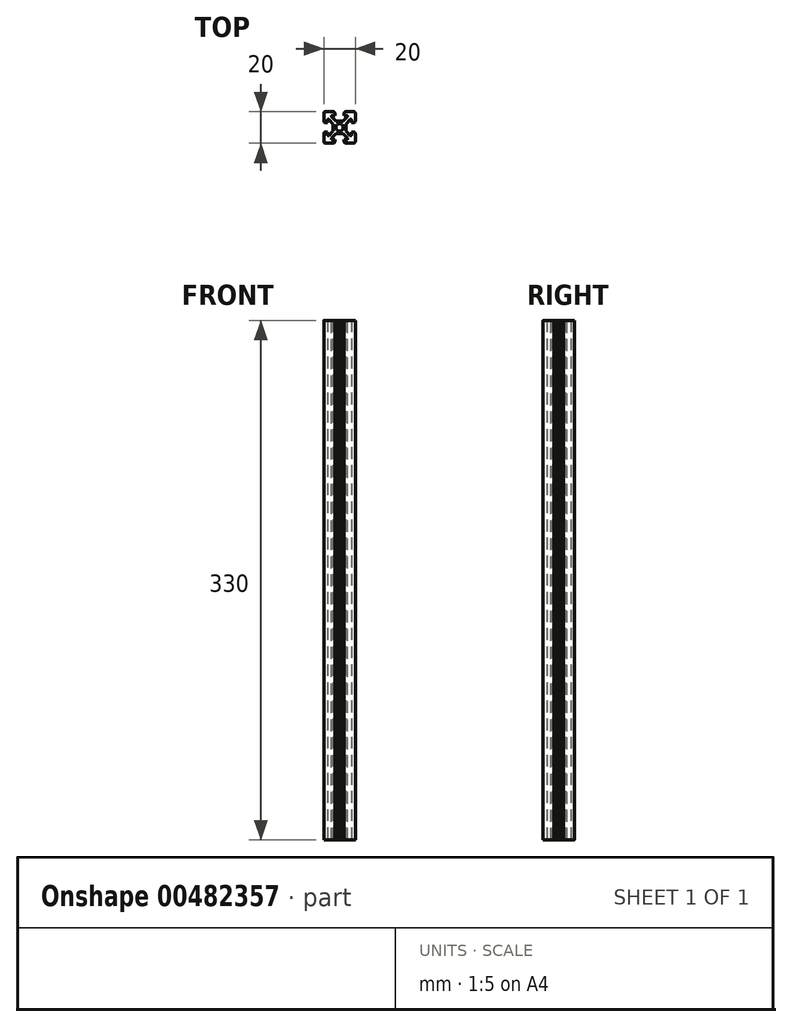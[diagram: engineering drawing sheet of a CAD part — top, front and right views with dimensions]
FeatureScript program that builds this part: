
annotation { "Feature Type Name" : "Feature", "Feature Type Description" : "" }
export const myFeature = defineFeature(function(context is Context, id is Id, definition is map)
    precondition{}
    {
        {
            var Q0;
            Q0=qCreatedBy(makeId("Top.planeOp"),FACE);
            var sketch = newSketch(context, id + "F0", { "sketchPlane" : qUnion([Q0])});
            skLineSegment(sketch, "E0", {"start": v(-15.81, 0) * mm, "end": v(2.4, 0) * mm, "construction": true});
            skLineSegment(sketch, "E1", {"start": v(0, 15.89) * mm, "end": v(0, -13.7) * mm, "construction": true});
            skLineSegment(sketch, "E2", {"start": v(0, 0) * mm, "end": v(-1.66, 1.66) * mm, "construction": true});
            skLineSegment(sketch, "E3", {"start": v(-2.3, 4.06) * mm, "end": v(-5.86, 7.63) * mm});
            skLineSegment(sketch, "E4", {"start": v(-5.86, 7.63) * mm, "end": v(-3, 7.63) * mm});
            skLineSegment(sketch, "E5", {"start": v(-3, 7.63) * mm, "end": v(-3, 10) * mm});
            skLineSegment(sketch, "E6", {"start": v(-3, 10) * mm, "end": v(-10, 10) * mm});
            skLineSegment(sketch, "E7.MirrorCS", {"start": v(-4, 2.23) * mm, "end": v(-7.63, 5.86) * mm});
            skLineSegment(sketch, "E8.MirrorCS", {"start": v(-7.63, 3) * mm, "end": v(-10, 3) * mm});
            skLineSegment(sketch, "E9.MirrorCS", {"start": v(-10, 3) * mm, "end": v(-10, 10) * mm});
            skLineSegment(sketch, "E10.MirrorCS", {"start": v(-7.63, 5.86) * mm, "end": v(-7.63, 3) * mm});
            skLineSegment(sketch, "E11.MirrorCS", {"start": v(3, 10) * mm, "end": v(10, 10) * mm});
            skLineSegment(sketch, "E12.MirrorCS", {"start": v(5.86, 7.63) * mm, "end": v(3, 7.63) * mm});
            skLineSegment(sketch, "E13.MirrorCS", {"start": v(3, 7.63) * mm, "end": v(3, 10) * mm});
            skLineSegment(sketch, "E14.MirrorCS", {"start": v(7.63, 5.86) * mm, "end": v(7.63, 3) * mm});
            skLineSegment(sketch, "E15.MirrorCS", {"start": v(10, 3) * mm, "end": v(10, 10) * mm});
            skLineSegment(sketch, "E16.MirrorCS", {"start": v(7.63, 3) * mm, "end": v(10, 3) * mm});
            skLineSegment(sketch, "E17.MirrorCS", {"start": v(2.3, 4.06) * mm, "end": v(5.86, 7.63) * mm});
            skLineSegment(sketch, "E18.MirrorCS", {"start": v(4, 2.23) * mm, "end": v(7.63, 5.86) * mm});
            skLineSegment(sketch, "E19.MirrorCS", {"start": v(5.86, -7.63) * mm, "end": v(3, -7.63) * mm});
            skLineSegment(sketch, "E20.MirrorCS", {"start": v(3, -10) * mm, "end": v(10, -10) * mm});
            skLineSegment(sketch, "E21.MirrorCS", {"start": v(-5.86, -7.63) * mm, "end": v(-3, -7.63) * mm});
            skLineSegment(sketch, "E22.MirrorCS", {"start": v(-3, -10) * mm, "end": v(-10, -10) * mm});
            skLineSegment(sketch, "E23.MirrorCS", {"start": v(-3, -7.63) * mm, "end": v(-3, -10) * mm});
            skLineSegment(sketch, "E24.MirrorCS", {"start": v(3, -7.63) * mm, "end": v(3, -10) * mm});
            skLineSegment(sketch, "E25.MirrorCS", {"start": v(7.63, -5.86) * mm, "end": v(7.63, -3) * mm});
            skLineSegment(sketch, "E26.MirrorCS", {"start": v(10, -3) * mm, "end": v(10, -10) * mm});
            skLineSegment(sketch, "E27.MirrorCS", {"start": v(4, -2.23) * mm, "end": v(7.63, -5.86) * mm});
            skLineSegment(sketch, "E28.MirrorCS", {"start": v(-7.63, -5.86) * mm, "end": v(-7.63, -3) * mm});
            skLineSegment(sketch, "E29.MirrorCS", {"start": v(-10, -3) * mm, "end": v(-10, -10) * mm});
            skLineSegment(sketch, "E30.MirrorCS", {"start": v(-7.63, -3) * mm, "end": v(-10, -3) * mm});
            skLineSegment(sketch, "E31.MirrorCS", {"start": v(-4, -2.23) * mm, "end": v(-7.63, -5.86) * mm});
            skLineSegment(sketch, "E32.MirrorCS", {"start": v(2.23, -4) * mm, "end": v(5.86, -7.63) * mm});
            skLineSegment(sketch, "E33.MirrorCS", {"start": v(-2.23, -4) * mm, "end": v(-5.86, -7.63) * mm});
            skLineSegment(sketch, "E34.MirrorCS", {"start": v(7.63, -3) * mm, "end": v(10, -3) * mm});
            skLineSegment(sketch, "E35", {"start": v(-4, 0) * mm, "end": v(-4, 0) * mm});
            skLineSegment(sketch, "E36", {"start": v(-2.3, 4.06) * mm, "end": v(-0.02, 4.06) * mm});
            skLineSegment(sketch, "E37.MirrorCS", {"start": v(-15.81, 8.12) * mm, "end": v(21.32, 8.12) * mm, "construction": true});
            skLineSegment(sketch, "E38", {"start": v(-4, 2.23) * mm, "end": v(-4, 0.02) * mm});
            skLineSegment(sketch, "E39", {"start": v(-2.23, -4) * mm, "end": v(-0.05, -4) * mm});
            skLineSegment(sketch, "E40", {"start": v(4, 2.23) * mm, "end": v(4, 0.03) * mm});
            skPoint(sketch, "E41.orphan", {"position": v(-0.59, 2.36) * mm});
            skPoint(sketch, "E42.orphan", {"position": v(-2.36, 0.59) * mm});
            skLineSegment(sketch, "E43.trimOffspring", {"start": v(0.03, 4.06) * mm, "end": v(2.3, 4.06) * mm});
            skPoint(sketch, "E44.orphan", {"position": v(0.59, 2.36) * mm});
            skPoint(sketch, "E45.orphan", {"position": v(2.36, 0.59) * mm});
            skPoint(sketch, "E46.orphan", {"position": v(-2.36, -0.59) * mm});
            skPoint(sketch, "E47.orphan", {"position": v(-0.59, -2.36) * mm});
            skPoint(sketch, "E48.orphan", {"position": v(0.59, -2.36) * mm});
            skPoint(sketch, "E49.orphan", {"position": v(2.36, -0.59) * mm});
            skLineSegment(sketch, "E50", {"start": v(-2.4, 0.03) * mm, "end": v(-2.4, 0.03) * mm});
            skLineSegment(sketch, "E51.MirrorCS", {"start": v(-2.4, -0.03) * mm, "end": v(-2.4, -0.03) * mm});
            skLineSegment(sketch, "E52.MirrorCS", {"start": v(2.4, 0.03) * mm, "end": v(2.4, 0.03) * mm});
            skLineSegment(sketch, "E53.MirrorCS", {"start": v(2.4, -0.03) * mm, "end": v(2.4, -0.03) * mm});
            skLineSegment(sketch, "E54.trimOffspring", {"start": v(4, -0.03) * mm, "end": v(4, -2.23) * mm});
            skLineSegment(sketch, "E55.trimOffspring", {"start": v(-4, -0.03) * mm, "end": v(-4, -2.23) * mm});
            skPoint(sketch, "E56.end.orphan", {"position": v(-2.4, 0) * mm});
            skPoint(sketch, "E57.orphan", {"position": v(-4, 0.03) * mm});
            skPoint(sketch, "E58.MirrorCS.end.orphan", {"position": v(2.4, 0) * mm});
            skPoint(sketch, "E58.MirrorCS.start.orphan", {"position": v(2.4, -0.03) * mm});
            skPoint(sketch, "E59.MirrorCS.start.orphan", {"position": v(2.4, 0.03) * mm});
            skLineSegment(sketch, "E60.trimOffspring", {"start": v(0.05, -4) * mm, "end": v(2.23, -4) * mm});
            skLineSegment(sketch, "E61", {"start": v(0, 0) * mm, "end": v(10, 10) * mm, "construction": true});
            skLineSegment(sketch, "E62", {"start": v(0, 0) * mm, "end": v(-10, -10) * mm, "construction": true});
            skLineSegment(sketch, "E63", {"start": v(10, -10) * mm, "end": v(0.07, 0.07) * mm, "construction": true});
            skPoint(sketch, "E64.start.orphan", {"position": v(-4, -0.03) * mm});
            skLineSegment(sketch, "E65", {"start": v(-2.82, -0.78) * mm, "end": v(-1.9, -1.37) * mm});
            skPoint(sketch, "E66.orphan", {"position": v(-1.66, -1.66) * mm});
            skPoint(sketch, "E67.orphan", {"position": v(0.03, -4.06) * mm});
            skPoint(sketch, "E68.orphan", {"position": v(-0.03, -4.06) * mm});
            skLineSegment(sketch, "E69", {"start": v(-2.82, 0.8) * mm, "end": v(-1.87, 1.41) * mm});
            skLineSegment(sketch, "E70", {"start": v(-0.76, 2.95) * mm, "end": v(-1.54, 1.77) * mm});
            skLineSegment(sketch, "E71", {"start": v(0.76, 2.95) * mm, "end": v(1.51, 1.8) * mm});
            skLineSegment(sketch, "E72", {"start": v(2.82, 0.8) * mm, "end": v(1.83, 1.46) * mm});
            skLineSegment(sketch, "E73", {"start": v(2.82, -0.8) * mm, "end": v(1.87, -1.41) * mm});
            skLineSegment(sketch, "E74.trimOffspring", {"start": v(1.8, -1.68) * mm, "end": v(1.82, -1.66) * mm});
            skLineSegment(sketch, "E75.trimOffspring", {"start": v(-8.12, 8.12) * mm, "end": v(-29.35, 29.35) * mm, "construction": true});
            skLineSegment(sketch, "E76", {"start": v(0.74, -2.96) * mm, "end": v(1.51, -1.8) * mm});
            skPoint(sketch, "E77.trimOffspring.start.orphan", {"position": v(0.33, -2.4) * mm});
            skPoint(sketch, "E78.MirrorCS.end.orphan", {"position": v(-0.33, -2.4) * mm});
            skLineSegment(sketch, "E79.trimOffspring", {"start": v(2.43, 0) * mm, "end": v(21.32, 0) * mm, "construction": true});
            skPoint(sketch, "E80.trimOffspring.start.orphan", {"position": v(0.33, 2.4) * mm});
            skPoint(sketch, "E81.trimOffspring.start.orphan", {"position": v(-0.33, 2.4) * mm});
            skArc(sketch, "E82", {"start": v(-1.87, 1.41) * mm, "mid": v(-2.35, 0.03) * mm, "end": v(-1.9, -1.37) * mm});
            skArc(sketch, "E83.trimOffspring", {"start": v(1.51, 1.8) * mm, "mid": v(-0.02, 2.35) * mm, "end": v(-1.54, 1.77) * mm});
            skArc(sketch, "E84.trimOffspring", {"start": v(1.87, -1.41) * mm, "mid": v(2.35, 0.03) * mm, "end": v(1.83, 1.46) * mm});
            skArc(sketch, "E85.trimOffspring", {"start": v(-1.55, -1.76) * mm, "mid": v(-0.03, -2.35) * mm, "end": v(1.51, -1.8) * mm});
            skLineSegment(sketch, "E86", {"start": v(-1.55, -1.76) * mm, "end": v(-0.75, -2.96) * mm});
            skLineSegment(sketch, "E87", {"start": v(-4, 0.03) * mm, "end": v(-2.82, 0.03) * mm});
            skLineSegment(sketch, "E88", {"start": v(-2.82, 0.03) * mm, "end": v(-2.82, 0.8) * mm});
            skLineSegment(sketch, "E89", {"start": v(-4, -0.03) * mm, "end": v(-2.82, -0.03) * mm});
            skLineSegment(sketch, "E90", {"start": v(-2.82, -0.03) * mm, "end": v(-2.82, -0.78) * mm});
            skLineSegment(sketch, "E91.MirrorCS", {"start": v(4, 0.03) * mm, "end": v(2.82, 0.03) * mm});
            skLineSegment(sketch, "E92.MirrorCS", {"start": v(4, -0.03) * mm, "end": v(2.82, -0.03) * mm});
            skLineSegment(sketch, "E93", {"start": v(2.82, 0.03) * mm, "end": v(2.82, 0.8) * mm});
            skLineSegment(sketch, "E94", {"start": v(2.82, -0.03) * mm, "end": v(2.82, -0.8) * mm});
            skLineSegment(sketch, "E95", {"start": v(-0.05, -4) * mm, "end": v(-0.05, -2.96) * mm});
            skLineSegment(sketch, "E96", {"start": v(-0.05, -2.96) * mm, "end": v(-0.75, -2.96) * mm});
            skLineSegment(sketch, "E97", {"start": v(0.05, -4) * mm, "end": v(0.05, -2.96) * mm});
            skLineSegment(sketch, "E98", {"start": v(0.05, -2.96) * mm, "end": v(0.74, -2.96) * mm});
            skLineSegment(sketch, "E99", {"start": v(-0.02, 4.06) * mm, "end": v(-0.02, 2.95) * mm});
            skLineSegment(sketch, "E100", {"start": v(-0.02, 2.95) * mm, "end": v(-0.76, 2.95) * mm});
            skLineSegment(sketch, "E101", {"start": v(0.03, 4.06) * mm, "end": v(0.03, 2.95) * mm});
            skLineSegment(sketch, "E102", {"start": v(0.03, 2.95) * mm, "end": v(0.76, 2.95) * mm});
            skSolve(sketch);
        }
        {
            var Q0;
            Q0 = qSketchRegion(id + "F0", true);
            extrude(context, id + "F1", {"entities" : qUnion([Q0]), "depth" : 330 * mm});
        }
        {
            var Q0;
            Q0=makeQuery(id+"F1.opExtrude","SWEPT_EDGE",EDGE,{"disambiguationData":[OSD([sQuery(id+"F0.wireOp",EDGE,"E15.MirrorCS"),sQuery(id+"F0.wireOp",EDGE,"E11.MirrorCS")])]});
            var Q1;
            Q1=makeQuery(id+"F1.opExtrude","SWEPT_EDGE",EDGE,{"disambiguationData":[OSD([sQuery(id+"F0.wireOp",EDGE,"E20.MirrorCS"),sQuery(id+"F0.wireOp",EDGE,"E26.MirrorCS")])]});
            var Q2;
            Q2=makeQuery(id+"F1.opExtrude","SWEPT_EDGE",EDGE,{"disambiguationData":[OSD([sQuery(id+"F0.wireOp",EDGE,"E22.MirrorCS"),sQuery(id+"F0.wireOp",EDGE,"E29.MirrorCS")])]});
            var Q3;
            Q3=makeQuery(id+"F1.opExtrude","SWEPT_EDGE",EDGE,{"disambiguationData":[OSD([sQuery(id+"F0.wireOp",EDGE,"E22.MirrorCS"),sQuery(id+"F0.wireOp",EDGE,"E23.MirrorCS")])]});
            var Q4;
            Q4=makeQuery(id+"F1.opExtrude","SWEPT_EDGE",EDGE,{"disambiguationData":[OSD([sQuery(id+"F0.wireOp",EDGE,"E20.MirrorCS"),sQuery(id+"F0.wireOp",EDGE,"E24.MirrorCS")])]});
            var Q5;
            Q5=makeQuery(id+"F1.opExtrude","SWEPT_EDGE",EDGE,{"disambiguationData":[OSD([sQuery(id+"F0.wireOp",EDGE,"E5"),sQuery(id+"F0.wireOp",EDGE,"E6")])]});
            var Q6;
            Q6=makeQuery(id+"F1.opExtrude","SWEPT_EDGE",EDGE,{"disambiguationData":[OSD([sQuery(id+"F0.wireOp",EDGE,"E8.MirrorCS"),sQuery(id+"F0.wireOp",EDGE,"E9.MirrorCS")])]});
            var Q7;
            Q7=makeQuery(id+"F1.opExtrude","SWEPT_EDGE",EDGE,{"disambiguationData":[OSD([sQuery(id+"F0.wireOp",EDGE,"E15.MirrorCS"),sQuery(id+"F0.wireOp",EDGE,"E16.MirrorCS")])]});
            var Q8;
            Q8=makeQuery(id+"F1.opExtrude","SWEPT_EDGE",EDGE,{"disambiguationData":[OSD([sQuery(id+"F0.wireOp",EDGE,"E26.MirrorCS"),sQuery(id+"F0.wireOp",EDGE,"E34.MirrorCS")])]});
            var Q9;
            Q9=makeQuery(id+"F1.opExtrude","SWEPT_EDGE",EDGE,{"disambiguationData":[OSD([sQuery(id+"F0.wireOp",EDGE,"E29.MirrorCS"),sQuery(id+"F0.wireOp",EDGE,"E30.MirrorCS")])]});
            var Q10;
            Q10=makeQuery(id+"F1.opExtrude","SWEPT_EDGE",EDGE,{"disambiguationData":[OSD([sQuery(id+"F0.wireOp",EDGE,"E9.MirrorCS"),sQuery(id+"F0.wireOp",EDGE,"E6")])]});
            var Q11;
            Q11=makeQuery(id+"F1.opExtrude","SWEPT_EDGE",EDGE,{"disambiguationData":[OSD([sQuery(id+"F0.wireOp",EDGE,"E13.MirrorCS"),sQuery(id+"F0.wireOp",EDGE,"E11.MirrorCS")])]});
            fillet(context, id + "F2", {"entities" : qUnion([Q0, Q1, Q2, Q3, Q4, Q5, Q6, Q7, Q8, Q9, Q10, Q11]), "radius" : 1 * mm, "tangentPropagation" : true, "allowEdgeOverflow" : false});
        }
        {
            var Q0;
            Q0=makeQuery(id+"F1.opExtrude","SWEPT_EDGE",EDGE,{"disambiguationData":[OSD([sQuery(id+"F0.wireOp",EDGE,"E7.MirrorCS"),sQuery(id+"F0.wireOp",EDGE,"E10.MirrorCS")])]});
            var Q1;
            Q1=makeQuery(id+"F1.opExtrude","SWEPT_EDGE",EDGE,{"disambiguationData":[OSD([sQuery(id+"F0.wireOp",EDGE,"E3"),sQuery(id+"F0.wireOp",EDGE,"E4")])]});
            var Q2;
            Q2=makeQuery(id+"F1.opExtrude","SWEPT_EDGE",EDGE,{"disambiguationData":[OSD([sQuery(id+"F0.wireOp",EDGE,"E12.MirrorCS"),sQuery(id+"F0.wireOp",EDGE,"E17.MirrorCS")])]});
            var Q3;
            Q3=makeQuery(id+"F1.opExtrude","SWEPT_EDGE",EDGE,{"disambiguationData":[OSD([sQuery(id+"F0.wireOp",EDGE,"E14.MirrorCS"),sQuery(id+"F0.wireOp",EDGE,"E18.MirrorCS")])]});
            var Q4;
            Q4=makeQuery(id+"F1.opExtrude","SWEPT_EDGE",EDGE,{"disambiguationData":[OSD([sQuery(id+"F0.wireOp",EDGE,"E28.MirrorCS"),sQuery(id+"F0.wireOp",EDGE,"E31.MirrorCS")])]});
            var Q5;
            Q5=makeQuery(id+"F1.opExtrude","SWEPT_EDGE",EDGE,{"disambiguationData":[OSD([sQuery(id+"F0.wireOp",EDGE,"E21.MirrorCS"),sQuery(id+"F0.wireOp",EDGE,"E33.MirrorCS")])]});
            var Q6;
            Q6=makeQuery(id+"F1.opExtrude","SWEPT_EDGE",EDGE,{"disambiguationData":[OSD([sQuery(id+"F0.wireOp",EDGE,"E19.MirrorCS"),sQuery(id+"F0.wireOp",EDGE,"E32.MirrorCS")])]});
            var Q7;
            Q7=makeQuery(id+"F1.opExtrude","SWEPT_EDGE",EDGE,{"disambiguationData":[OSD([sQuery(id+"F0.wireOp",EDGE,"E25.MirrorCS"),sQuery(id+"F0.wireOp",EDGE,"E27.MirrorCS")])]});
            fillet(context, id + "F3", {"entities" : qUnion([Q0, Q1, Q2, Q3, Q4, Q5, Q6, Q7]), "radius" : .5 * mm, "tangentPropagation" : true, "allowEdgeOverflow" : false});
        }
        {
            var Q0;
            Q0=makeQuery(id+"F1.opExtrude","SWEPT_EDGE",EDGE,{"disambiguationData":[OSD([sQuery(id+"F0.wireOp",EDGE,"E69"),sQuery(id+"F0.wireOp",EDGE,"E82")])]});
            var Q1;
            Q1=makeQuery(id+"F1.opExtrude","SWEPT_EDGE",EDGE,{"disambiguationData":[OSD([sQuery(id+"F0.wireOp",EDGE,"E17.MirrorCS"),sQuery(id+"F0.wireOp",EDGE,"E43.trimOffspring")])]});
            var Q2;
            {var subQ0=sQuery(id+"F0.wireOp",EDGE,"E12.MirrorCS");Q2=makeQuery(id+"F3.opFillet","BLEND_EDGE",EDGE,{"blendedFrom":[makeQuery(id+"F1.opExtrude","SWEPT_EDGE",EDGE,{"disambiguationData":[OSD([subQ0,sQuery(id+"F0.wireOp",EDGE,"E17.MirrorCS")])]}),makeQuery(id+"F1.opExtrude","SWEPT_FACE",FACE,{"disambiguationData":[OSD([subQ0])]})],"blendedInto":[makeQuery(id+"F1.opExtrude","SWEPT_FACE",FACE,{"disambiguationData":[OSD([subQ0])]})]});}
            var Q3;
            Q3=makeQuery(id+"F1.opExtrude","SWEPT_EDGE",EDGE,{"disambiguationData":[OSD([sQuery(id+"F0.wireOp",EDGE,"E70"),sQuery(id+"F0.wireOp",EDGE,"E83.trimOffspring")])]});
            var Q4;
            Q4=makeQuery(id+"F1.opExtrude","SWEPT_EDGE",EDGE,{"disambiguationData":[OSD([sQuery(id+"F0.wireOp",EDGE,"VnvyymTW-JKNP-Vp1J-SOXt-zXPDHYCny5Fm"),sQuery(id+"F0.wireOp",EDGE,"E85.trimOffspring")])]});
            var Q5;
            Q5=makeQuery(id+"F1.opExtrude","SWEPT_EDGE",EDGE,{"disambiguationData":[OSD([sQuery(id+"F0.wireOp",EDGE,"E76"),sQuery(id+"F0.wireOp",EDGE,"E85.trimOffspring")])]});
            var Q6;
            Q6=makeQuery(id+"F1.opExtrude","SWEPT_EDGE",EDGE,{"disambiguationData":[OSD([sQuery(id+"F0.wireOp",EDGE,"E73"),sQuery(id+"F0.wireOp",EDGE,"E84.trimOffspring")])]});
            var Q7;
            Q7=makeQuery(id+"F1.opExtrude","SWEPT_EDGE",EDGE,{"disambiguationData":[OSD([sQuery(id+"F0.wireOp",EDGE,"E72"),sQuery(id+"F0.wireOp",EDGE,"E84.trimOffspring")])]});
            var Q8;
            Q8=makeQuery(id+"F1.opExtrude","SWEPT_EDGE",EDGE,{"disambiguationData":[OSD([sQuery(id+"F0.wireOp",EDGE,"E71"),sQuery(id+"F0.wireOp",EDGE,"E83.trimOffspring")])]});
            var Q9;
            Q9=makeQuery(id+"F1.opExtrude","SWEPT_EDGE",EDGE,{"disambiguationData":[OSD([sQuery(id+"F0.wireOp",EDGE,"E65"),sQuery(id+"F0.wireOp",EDGE,"E82")])]});
            fillet(context, id + "F4", {"entities" : qUnion([Q0, Q1, Q2, Q3, Q4, Q5, Q6, Q7, Q8, Q9]), "radius" : .1 * mm, "tangentPropagation" : true, "allowEdgeOverflow" : false});
        }
    });
